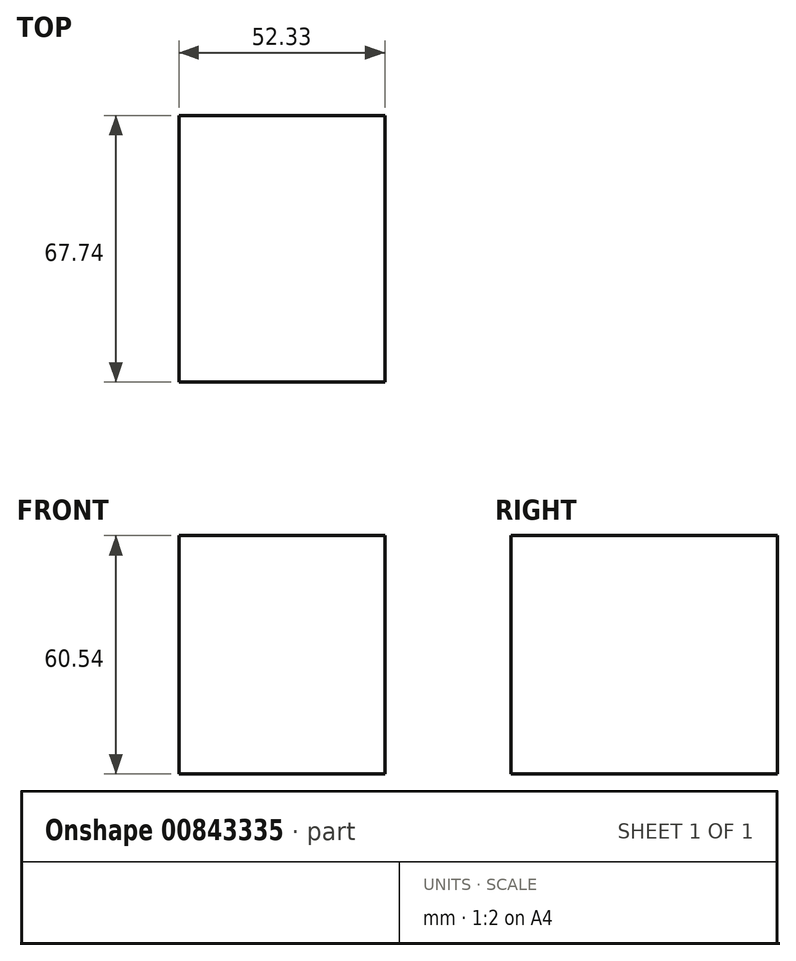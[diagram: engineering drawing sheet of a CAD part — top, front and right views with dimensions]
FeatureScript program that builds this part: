
annotation { "Feature Type Name" : "Feature", "Feature Type Description" : "" }
export const myFeature = defineFeature(function(context is Context, id is Id, definition is map)
    precondition{}
    {
        {
            var Q0;
            Q0=qCreatedBy(makeId("Top.planeOp"),FACE);
            var sketch = newSketch(context, id + "F0", { "sketchPlane" : qUnion([Q0])});
            skLineSegment(sketch, "E0.bottom", {"start": v(-52.33, 0) * mm, "end": v(0, 0) * mm});
            skLineSegment(sketch, "E0.top", {"start": v(-52.33, 67.74) * mm, "end": v(0, 67.74) * mm});
            skLineSegment(sketch, "E0.left", {"start": v(-52.33, 0) * mm, "end": v(-52.33, 67.74) * mm});
            skLineSegment(sketch, "E0.right", {"start": v(0, 0) * mm, "end": v(0, 67.74) * mm});
            skSolve(sketch);
        }
        {
            var Q0;
            Q0=makeQuery(id+"F0.imprint","IMPRINT",FACE,{"disambiguationData":[TD([[makeQuery(id+"F0.imprint","IMPRINT",EDGE,{"derivedFrom":sQuery(id+"F0.wireOp",EDGE,"E0.bottom")}),1.0]])]});
            extrude(context, id + "F1", {"entities" : qUnion([Q0]), "depth" : 60.54 * mm, "offsetDistance" : 25.4 * mm});
        }
    });
